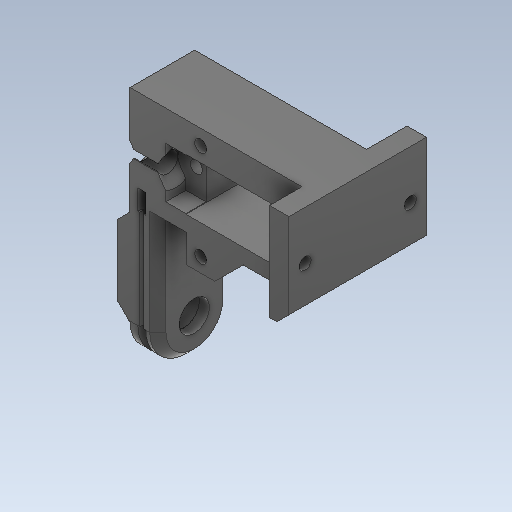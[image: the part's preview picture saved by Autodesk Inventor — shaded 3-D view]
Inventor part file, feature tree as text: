
AUTODESK INVENTOR PART (.ipt)
format: ipt  version: 2020 (Build 240168000, 168)  size: 480,768 bytes
history: native  units: in
note: dims shown in document units (in); Inventor stores cm internally (conversion verified against a paired STEP export)
features: sketch x38, other x3, plane x1
ambient origin geometry x8: Origin, YZ Plane, XZ Plane, XY Plane, X Axis, Y Axis, Z Axis, Center Point
bodies: Solid1 (feature_tree)
feature tree (42):
  other  "FermurSupport.ipt"
  other  "Solid1::FermurSupport.ipt"
  other  "TaggingFeature1"
  sketch  "Sketch1"  dims[d0=0.3937in]
  sketch  "Sketch2"
  sketch  "Sketch3"
  sketch  "Sketch4"
  sketch  "Sketch5"
  sketch  "Sketch6"
  sketch  "Sketch8"
  sketch  "Sketch10"
  sketch  "Sketch11"
  sketch  "Sketch12"
  sketch  "Sketch13"
  sketch  "Sketch14"
  sketch  "Sketch15"
  sketch  "Sketch17"
  sketch  "Sketch19"
  sketch  "Sketch21"
  sketch  "Sketch22"
  sketch  "Sketch23"
  sketch  "Sketch26"
  sketch  "Sketch27"
  sketch  "Sketch29"
  sketch  "Sketch32"
  sketch  "Sketch33"
  sketch  "Sketch36"
  sketch  "Sketch37"
  sketch  "Sketch38"
  sketch  "Sketch39"
  sketch  "Sketch41"
  sketch  "Sketch42"
  sketch  "Sketch43"
  sketch  "Sketch44"
  sketch  "Sketch45"
  sketch  "Sketch46"
  sketch  "Sketch47"
  sketch  "Sketch48"
  sketch  "Sketch49"
  sketch  "Sketch50"
  sketch  "Sketch51"
  plane  "Work Plane1"
